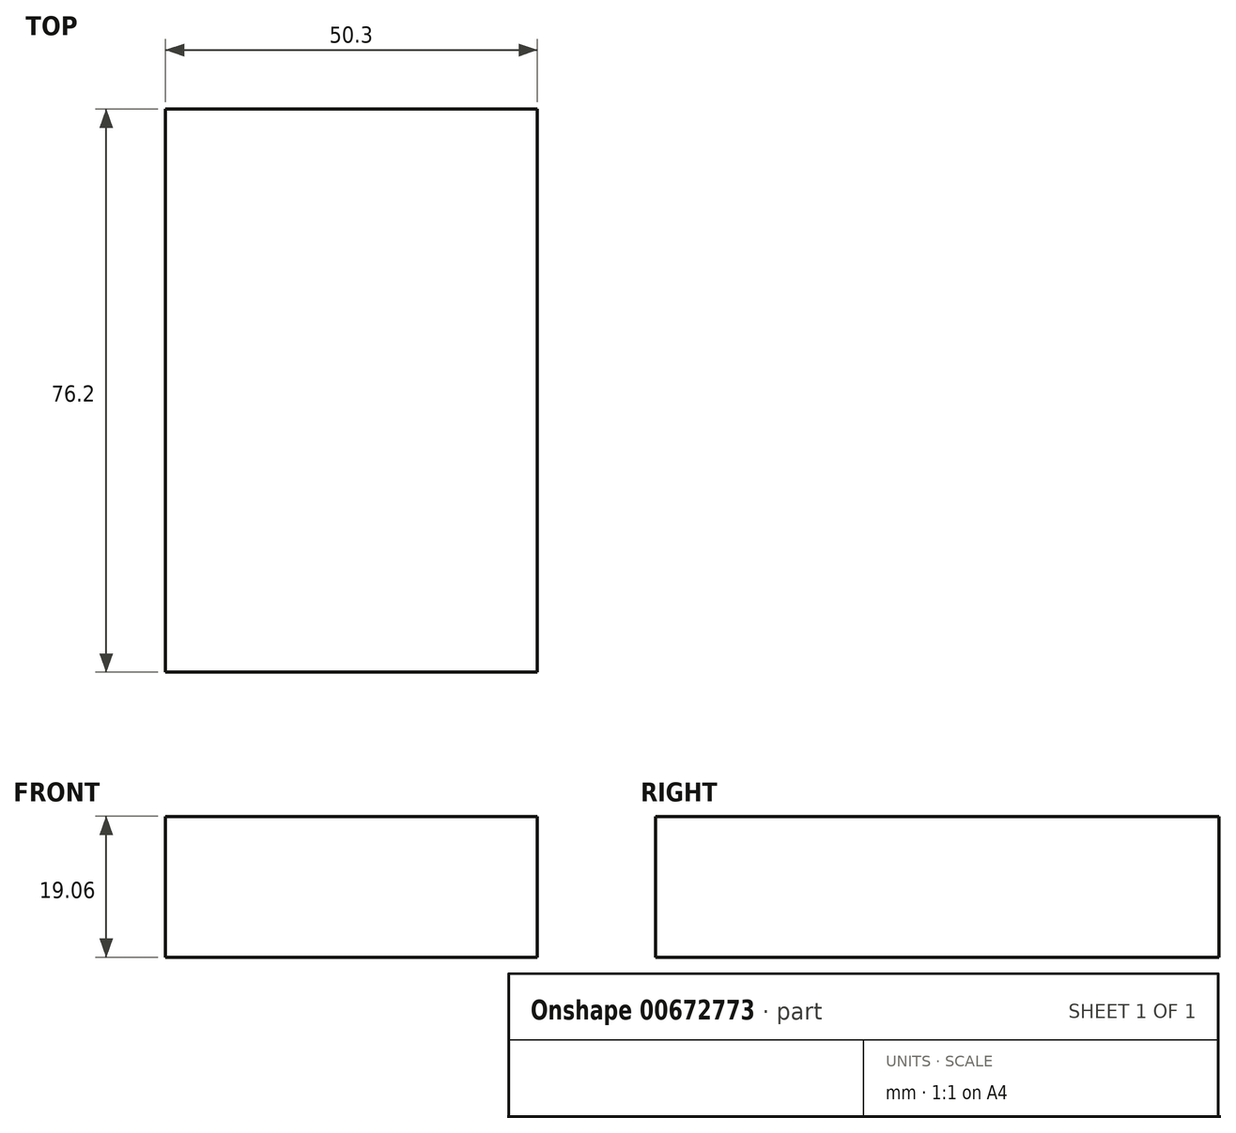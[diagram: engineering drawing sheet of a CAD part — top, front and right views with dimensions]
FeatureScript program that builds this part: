
annotation { "Feature Type Name" : "Feature", "Feature Type Description" : "" }
export const myFeature = defineFeature(function(context is Context, id is Id, definition is map)
    precondition{}
    {
        {
            var Q0;
            Q0=qCreatedBy(makeId("Front.planeOp"),FACE);
            var sketch = newSketch(context, id + "F0", { "sketchPlane" : qUnion([Q0])});
            skLineSegment(sketch, "E0.bottom", {"start": v(-25.15, 9.53) * mm, "end": v(25.15, 9.53) * mm});
            skLineSegment(sketch, "E0.top", {"start": v(-25.15, -9.53) * mm, "end": v(25.15, -9.53) * mm});
            skLineSegment(sketch, "E0.left", {"start": v(-25.15, 9.53) * mm, "end": v(-25.15, -9.53) * mm});
            skLineSegment(sketch, "E0.right", {"start": v(25.15, 9.53) * mm, "end": v(25.15, -9.53) * mm});
            skPoint(sketch, "E0.middle", {"position": v(0, 0) * mm});
            skLineSegment(sketch, "E1.bottom", {"start": v(31.14, 25.58) * mm, "end": v(41.85, 25.58) * mm});
            skLineSegment(sketch, "E1.top", {"start": v(31.14, 48.27) * mm, "end": v(41.85, 48.27) * mm});
            skLineSegment(sketch, "E1.left", {"start": v(31.14, 25.58) * mm, "end": v(31.14, 48.27) * mm});
            skLineSegment(sketch, "E1.right", {"start": v(41.85, 25.58) * mm, "end": v(41.85, 48.27) * mm});
            skPoint(sketch, "E1.middle", {"position": v(36.5, 36.92) * mm});
            skLineSegment(sketch, "E2", {"start": v(25.15, 9.53) * mm, "end": v(25.15, 16.8) * mm});
            skArc(sketch, "E3", {"start": v(25.15, 16.8) * mm, "mid": v(26.8, 22.12) * mm, "end": v(31.14, 25.58) * mm});
            skArc(sketch, "E4.0", {"start": v(12.45, 16.8) * mm, "mid": v(15.96, 28.76) * mm, "end": v(25.38, 36.92) * mm});
            skLineSegment(sketch, "E4.1", {"start": v(12.45, 9.53) * mm, "end": v(12.45, 16.8) * mm});
            skLineSegment(sketch, "E5", {"start": v(25.38, 36.92) * mm, "end": v(36.5, 36.92) * mm});
            skSolve(sketch);
        }
        {
            var Q0;
            Q0=makeQuery(id+"F0.imprint","IMPRINT",FACE,{"disambiguationData":[TD([[makeQuery(id+"F0.imprint","IMPRINT",EDGE,{"derivedFrom":sQuery(id+"F0.wireOp",EDGE,"E0.top")}),1.0]])]});
            extrude(context, id + "F1", {"entities" : qUnion([Q0]), "endBound" : BoundingType.SYMMETRIC, "depth" : 76.2 * mm, "offsetDistance" : 25.4 * mm});
        }
    });
